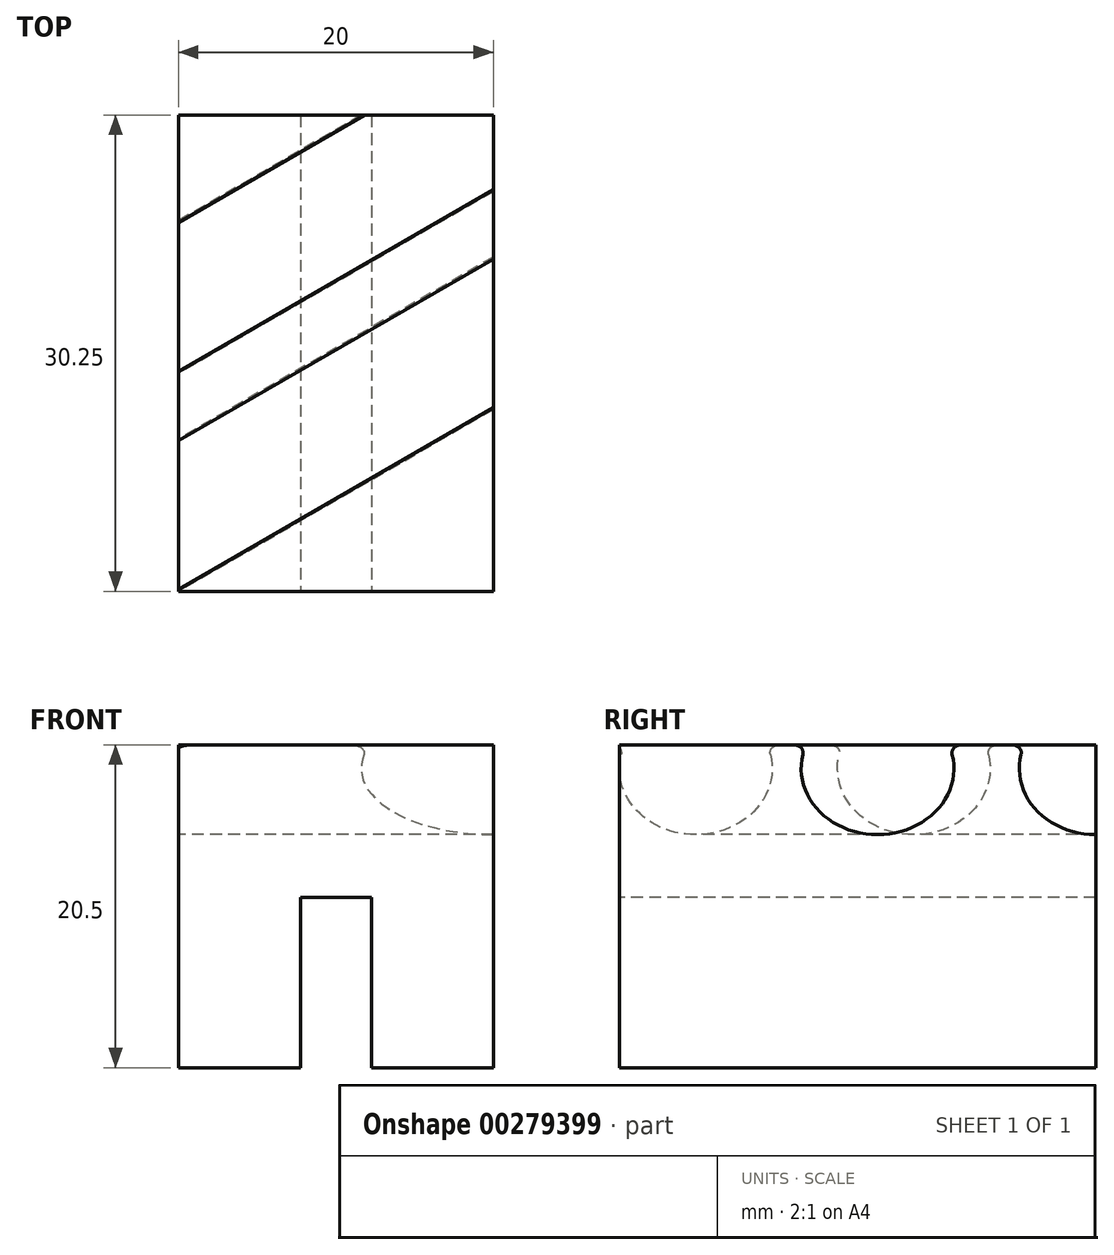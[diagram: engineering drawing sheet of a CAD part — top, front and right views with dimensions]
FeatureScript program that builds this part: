
annotation { "Feature Type Name" : "Feature", "Feature Type Description" : "" }
export const myFeature = defineFeature(function(context is Context, id is Id, definition is map)
    precondition{}
    {
        {
            var Q0;
            Q0=qCreatedBy(makeId("Top.planeOp"),FACE);
            var sketch = newSketch(context, id + "F0", { "sketchPlane" : qUnion([Q0])});
            skLineSegment(sketch, "E0.bottom", {"start": v(-21.55, 28.9) * mm, "end": v(-1.55, 28.9) * mm});
            skLineSegment(sketch, "E0.top", {"start": v(-21.55, -1.35) * mm, "end": v(-1.55, -1.35) * mm});
            skLineSegment(sketch, "E0.left", {"start": v(-21.55, 28.9) * mm, "end": v(-21.55, -1.35) * mm});
            skLineSegment(sketch, "E0.right", {"start": v(-1.55, 28.9) * mm, "end": v(-1.55, -1.35) * mm});
            skLineSegment(sketch, "E1", {"start": v(-34.85, 14.53) * mm, "end": v(0, 34.65) * mm});
            skLineSegment(sketch, "E2", {"start": v(0, 34.65) * mm, "end": v(2.1, 31.01) * mm});
            skLineSegment(sketch, "E3", {"start": v(2.1, 31.01) * mm, "end": v(-32.75, 10.89) * mm});
            skLineSegment(sketch, "E4", {"start": v(-32.75, 10.89) * mm, "end": v(-34.85, 14.53) * mm});
            skLineSegment(sketch, "E5", {"start": v(-21.55, 10.43) * mm, "end": v(-1.55, 21.97) * mm});
            skLineSegment(sketch, "E6.MirrorCS", {"start": v(8.1, 20.62) * mm, "end": v(-26.75, 0.5) * mm});
            skLineSegment(sketch, "E7.MirrorCS", {"start": v(-24.65, -3.14) * mm, "end": v(10.2, 16.98) * mm});
            skLineSegment(sketch, "E8.MirrorCS", {"start": v(10.2, 16.98) * mm, "end": v(8.1, 20.62) * mm});
            skLineSegment(sketch, "E9.MirrorCS", {"start": v(-26.75, 0.5) * mm, "end": v(-24.65, -3.14) * mm});
            skSolve(sketch);
        }
        {
            var Q0;
            {var subQ0=sQuery(id+"F0.wireOp",EDGE,"E0.left");var subQ1=sQuery(id+"F0.wireOp",EDGE,"E0.bottom");var subQ2=makeQuery(id+"F0.imprint","INTERSECT",VERTEX,{"derivedFrom":[subQ1,subQ0]});Q0=makeQuery(id+"F0.imprint","IMPRINT",FACE,{"disambiguationData":[TD([[makeQuery(id+"F0.imprint","IMPRINT",EDGE,{"disambiguationData":[TD([[subQ2,-1.0]])],"derivedFrom":subQ1}),-1.0]])]});}
            var Q1;
            {var subQ3=sQuery(id+"F0.wireOp",EDGE,"E1");var subQ5=sQuery(id+"F0.wireOp",EDGE,"E0.left");var subQ6=makeQuery(id+"F0.imprint","INTERSECT",VERTEX,{"derivedFrom":[subQ5,subQ3]});Q1=makeQuery(id+"F0.imprint","IMPRINT",FACE,{"disambiguationData":[TD([[makeQuery(id+"F0.imprint","IMPRINT",EDGE,{"disambiguationData":[TD([[subQ6,-1.0]])],"derivedFrom":subQ5}),1.0]])]});}
            var Q2;
            {var subQ0=sQuery(id+"F0.wireOp",EDGE,"E5");Q2=makeQuery(id+"F0.imprint","IMPRINT",FACE,{"disambiguationData":[TD([[makeQuery(id+"F0.imprint","IMPRINT",EDGE,{"derivedFrom":subQ0}),1.0]])]});}
            var Q3;
            {var subQ0=sQuery(id+"F0.wireOp",EDGE,"E5");Q3=makeQuery(id+"F0.imprint","IMPRINT",FACE,{"disambiguationData":[TD([[makeQuery(id+"F0.imprint","IMPRINT",EDGE,{"derivedFrom":subQ0}),-1.0]])]});}
            var Q4;
            {var subQ0=sQuery(id+"F0.wireOp",EDGE,"E6.MirrorCS");var subQ1=sQuery(id+"F0.wireOp",EDGE,"E0.top");var subQ2=makeQuery(id+"F0.imprint","INTERSECT",VERTEX,{"derivedFrom":[subQ1,subQ0]});Q4=makeQuery(id+"F0.imprint","IMPRINT",FACE,{"disambiguationData":[TD([[makeQuery(id+"F0.imprint","IMPRINT",EDGE,{"disambiguationData":[TD([[subQ2,-1.0]])],"derivedFrom":subQ1}),1.0]])]});}
            var Q5;
            {var subQ0=sQuery(id+"F0.wireOp",EDGE,"E0.right");var subQ1=sQuery(id+"F0.wireOp",EDGE,"E0.top");var subQ2=makeQuery(id+"F0.imprint","INTERSECT",VERTEX,{"derivedFrom":[subQ1,subQ0]});Q5=makeQuery(id+"F0.imprint","IMPRINT",FACE,{"disambiguationData":[TD([[makeQuery(id+"F0.imprint","IMPRINT",EDGE,{"disambiguationData":[TD([[subQ2,1.0]])],"derivedFrom":subQ1}),1.0]])]});}
            var Q6;
            {var subQ3=sQuery(id+"F0.wireOp",EDGE,"E6.MirrorCS");var subQ5=sQuery(id+"F0.wireOp",EDGE,"E0.right");var subQ6=makeQuery(id+"F0.imprint","INTERSECT",VERTEX,{"derivedFrom":[subQ5,subQ3]});Q6=makeQuery(id+"F0.imprint","IMPRINT",FACE,{"disambiguationData":[TD([[makeQuery(id+"F0.imprint","IMPRINT",EDGE,{"disambiguationData":[TD([[subQ6,-1.0]])],"derivedFrom":subQ5}),-1.0]])]});}
            extrude(context, id + "F1", {"entities" : qUnion([Q0, Q1, Q2, Q3, Q4, Q5, Q6]), "oppositeDirection" : true, "depth" : 24 * mm, "hasSecondDirection" : true, "secondDirectionOppositeDirection" : false, "secondDirectionDepth" : 1.5 * mm});
        }
        {
            var Q0;
            {var subQ5=sQuery(id+"F0.wireOp",EDGE,"E4");Q0=makeQuery(id+"F0.imprint","IMPRINT",FACE,{"disambiguationData":[TD([[makeQuery(id+"F0.imprint","IMPRINT",EDGE,{"derivedFrom":subQ5}),-1.0]])]});}
            var Q1;
            {var subQ3=sQuery(id+"F0.wireOp",EDGE,"E1");var subQ5=sQuery(id+"F0.wireOp",EDGE,"E0.left");var subQ6=makeQuery(id+"F0.imprint","INTERSECT",VERTEX,{"derivedFrom":[subQ5,subQ3]});Q1=makeQuery(id+"F0.imprint","IMPRINT",FACE,{"disambiguationData":[TD([[makeQuery(id+"F0.imprint","IMPRINT",EDGE,{"disambiguationData":[TD([[subQ6,-1.0]])],"derivedFrom":subQ5}),1.0]])]});}
            var Q2;
            {var subQ5=sQuery(id+"F0.wireOp",EDGE,"E2");Q2=makeQuery(id+"F0.imprint","IMPRINT",FACE,{"disambiguationData":[TD([[makeQuery(id+"F0.imprint","IMPRINT",EDGE,{"derivedFrom":subQ5}),-1.0]])]});}
            var Q3;
            Q3=sQuery(id+"F0.wireOp",EDGE,"E3");
            revolve(context, id + "F2", {"operationType" : NewBodyOperationType.REMOVE, "entities" : qUnion([Q0, Q1, Q2]), "axis" : qUnion([Q3]), "revolveType" : RevolveType.FULL, "oppositeDirection" : true});
        }
        {
            var Q0;
            {var subQ5=sQuery(id+"F0.wireOp",EDGE,"E9.MirrorCS");Q0=makeQuery(id+"F0.imprint","IMPRINT",FACE,{"disambiguationData":[TD([[makeQuery(id+"F0.imprint","IMPRINT",EDGE,{"derivedFrom":subQ5}),1.0]])]});}
            var Q1;
            {var subQ3=sQuery(id+"F0.wireOp",EDGE,"E6.MirrorCS");var subQ5=sQuery(id+"F0.wireOp",EDGE,"E0.right");var subQ6=makeQuery(id+"F0.imprint","INTERSECT",VERTEX,{"derivedFrom":[subQ5,subQ3]});Q1=makeQuery(id+"F0.imprint","IMPRINT",FACE,{"disambiguationData":[TD([[makeQuery(id+"F0.imprint","IMPRINT",EDGE,{"disambiguationData":[TD([[subQ6,-1.0]])],"derivedFrom":subQ5}),-1.0]])]});}
            var Q2;
            {var subQ5=sQuery(id+"F0.wireOp",EDGE,"E8.MirrorCS");Q2=makeQuery(id+"F0.imprint","IMPRINT",FACE,{"disambiguationData":[TD([[makeQuery(id+"F0.imprint","IMPRINT",EDGE,{"derivedFrom":subQ5}),1.0]])]});}
            var Q3;
            Q3=sQuery(id+"F0.wireOp",EDGE,"E6.MirrorCS");
            revolve(context, id + "F3", {"operationType" : NewBodyOperationType.REMOVE, "entities" : qUnion([Q0, Q1, Q2]), "axis" : qUnion([Q3]), "revolveType" : RevolveType.FULL, "oppositeDirection" : true});
        }
        {
            var Q0;
            Q0=makeQuery(id+"F2.boolean.opBoolean","INTERSECT",EDGE,{"disambiguationData":[OD(0.0)],"derivedFrom":[makeQuery(id+"F1.opExtrude","CAP_FACE",FACE,{"disambiguationData":[OSD([sQuery(id+"F0.wireOp",EDGE,"E0.bottom"),sQuery(id+"F0.wireOp",EDGE,"E0.top"),sQuery(id+"F0.wireOp",EDGE,"E0.left"),sQuery(id+"F0.wireOp",EDGE,"E0.right")])],"isStart":true}),makeQuery(id+"F2.opRevolve","SWEPT_FACE",FACE,{"disambiguationData":[OSD([sQuery(id+"F0.wireOp",EDGE,"E1")])]})]});
            var Q1;
            Q1=makeQuery(id+"F2.boolean.opBoolean","INTERSECT",EDGE,{"disambiguationData":[OD(1.0)],"derivedFrom":[makeQuery(id+"F1.opExtrude","CAP_FACE",FACE,{"disambiguationData":[OSD([sQuery(id+"F0.wireOp",EDGE,"E0.bottom"),sQuery(id+"F0.wireOp",EDGE,"E0.top"),sQuery(id+"F0.wireOp",EDGE,"E0.left"),sQuery(id+"F0.wireOp",EDGE,"E0.right")])],"isStart":true}),makeQuery(id+"F2.opRevolve","SWEPT_FACE",FACE,{"disambiguationData":[OSD([sQuery(id+"F0.wireOp",EDGE,"E1")])]})]});
            var Q2;
            {var subQ0=sQuery(id+"F0.wireOp",EDGE,"E0.top");var subQ1=sQuery(id+"F0.wireOp",EDGE,"E0.left");var subQ2=sQuery(id+"F0.wireOp",EDGE,"E0.right");Q2=makeQuery(id+"F3.boolean.opBoolean","INTERSECT",EDGE,{"disambiguationData":[OD(0.0)],"derivedFrom":[makeQuery(id+"F2.boolean.opBoolean","SPLIT",FACE,{"disambiguationData":[TD([makeQuery(id+"F1.opExtrude","SWEPT_FACE",FACE,{"disambiguationData":[OSD([subQ0])]})])],"derivedFrom":makeQuery(id+"F1.opExtrude","CAP_FACE",FACE,{"disambiguationData":[OSD([sQuery(id+"F0.wireOp",EDGE,"E0.bottom"),subQ0,subQ1,subQ2])],"isStart":true})}),makeQuery(id+"F3.opRevolve","SWEPT_FACE",FACE,{"disambiguationData":[OSD([sQuery(id+"F0.wireOp",EDGE,"E7.MirrorCS")])]})]});}
            var Q3;
            {var subQ0=sQuery(id+"F0.wireOp",EDGE,"E0.top");var subQ1=sQuery(id+"F0.wireOp",EDGE,"E0.left");var subQ2=sQuery(id+"F0.wireOp",EDGE,"E0.right");Q3=makeQuery(id+"F3.boolean.opBoolean","INTERSECT",EDGE,{"disambiguationData":[OD(1.0)],"derivedFrom":[makeQuery(id+"F2.boolean.opBoolean","SPLIT",FACE,{"disambiguationData":[TD([makeQuery(id+"F1.opExtrude","SWEPT_FACE",FACE,{"disambiguationData":[OSD([subQ0])]})])],"derivedFrom":makeQuery(id+"F1.opExtrude","CAP_FACE",FACE,{"disambiguationData":[OSD([sQuery(id+"F0.wireOp",EDGE,"E0.bottom"),subQ0,subQ1,subQ2])],"isStart":true})}),makeQuery(id+"F3.opRevolve","SWEPT_FACE",FACE,{"disambiguationData":[OSD([sQuery(id+"F0.wireOp",EDGE,"E7.MirrorCS")])]})]});}
            fillet(context, id + "F4", {"entities" : qUnion([Q0, Q1, Q2, Q3]), "radius" : .5 * mm, "tangentPropagation" : true, "allowEdgeOverflow" : false});
        }
        {
            var Q0;
            Q0=makeQuery(id+"F1.opExtrude","SWEPT_FACE",FACE,{"disambiguationData":[OSD([sQuery(id+"F0.wireOp",EDGE,"E0.top")])]});
            var sketch = newSketch(context, id + "F5", { "sketchPlane" : qUnion([Q0])});
            skLineSegment(sketch, "E10.bottom", {"start": v(-9.3, -26.7) * mm, "end": v(-13.8, -26.7) * mm});
            skLineSegment(sketch, "E10.top", {"start": v(-9.3, -8.2) * mm, "end": v(-13.8, -8.2) * mm});
            skLineSegment(sketch, "E10.left", {"start": v(-9.3, -26.7) * mm, "end": v(-9.3, -8.2) * mm});
            skLineSegment(sketch, "E10.right", {"start": v(-13.8, -26.7) * mm, "end": v(-13.8, -8.2) * mm});
            skPoint(sketch, "E10.middle", {"position": v(-11.55, -17.45) * mm});
            skPoint(sketch, "E10.middle.positionSnap0", {"position": v(-11.55, -24) * mm});
            skPoint(sketch, "E10.centerSnap0", {"position": v(-11.55, -24) * mm});
            skLineSegment(sketch, "E11.0", {"start": v(-21.55, 0.9) * mm, "end": v(-21.55, -4.2) * mm});
            skLineSegment(sketch, "E12", {"start": v(-13.8, -26.7) * mm, "end": v(-13.25, -24) * mm});
            skLineSegment(sketch, "E13", {"start": v(-9.3, -26.7) * mm, "end": v(-9.85, -24) * mm});
            skSolve(sketch);
        }
        {
            var Q0;
            Q0=makeQuery(id+"F5.imprint","IMPRINT",FACE,{"disambiguationData":[TD([[makeQuery(id+"F5.imprint","IMPRINT",EDGE,{"derivedFrom":sQuery(id+"F5.wireOp",EDGE,"E10.bottom")}),1.0]])]});
            var Q1;
            {var subQ4=sQuery(id+"F5.wireOp",EDGE,"E10.top");Q1=makeQuery(id+"F5.imprint","IMPRINT",FACE,{"disambiguationData":[TD([[makeQuery(id+"F5.imprint","IMPRINT",EDGE,{"derivedFrom":subQ4}),1.0]])]});}
            extrude(context, id + "F6", {"entities" : qUnion([Q0, Q1]), "operationType" : NewBodyOperationType.REMOVE, "oppositeDirection" : true, "depth" : 43.7 * mm});
        }
        {
            var Q0;
            {var subQ0=sQuery(id+"F0.wireOp",EDGE,"E0.bottom");var subQ1=sQuery(id+"F0.wireOp",EDGE,"E0.top");var subQ2=sQuery(id+"F0.wireOp",EDGE,"E0.left");Q0=makeQuery(id+"F6.boolean.opBoolean","SPLIT",FACE,{"disambiguationData":[TD([makeQuery(id+"F1.opExtrude","SWEPT_FACE",FACE,{"disambiguationData":[OSD([subQ2])]})])],"derivedFrom":makeQuery(id+"F1.opExtrude","CAP_FACE",FACE,{"disambiguationData":[OSD([subQ0,subQ1,subQ2,sQuery(id+"F0.wireOp",EDGE,"E0.right")])],"isStart":false})});}
            var Q1;
            {var subQ0=sQuery(id+"F0.wireOp",EDGE,"E0.bottom");var subQ1=sQuery(id+"F0.wireOp",EDGE,"E0.right");var subQ2=sQuery(id+"F0.wireOp",EDGE,"E0.top");Q1=makeQuery(id+"F6.boolean.opBoolean","SPLIT",FACE,{"disambiguationData":[TD([makeQuery(id+"F1.opExtrude","SWEPT_FACE",FACE,{"disambiguationData":[OSD([subQ1])]})])],"derivedFrom":makeQuery(id+"F1.opExtrude","CAP_FACE",FACE,{"disambiguationData":[OSD([subQ0,subQ2,sQuery(id+"F0.wireOp",EDGE,"E0.left"),subQ1])],"isStart":false})});}
            extrude(context, id + "F7", {"entities" : qUnion([Q0, Q1]), "operationType" : NewBodyOperationType.REMOVE, "oppositeDirection" : true, "depth" : 5 * mm});
        }
    });
